# Revit family: Drain_Trench-Zurn-Z874-U-9-HDG
name_source: partatom
category: Plumbing Fixtures
units: mm (PartAtom-declared; Revit-internal decimal feet)

## family parameters
Always vertical = Yes
Cut with Voids When Loaded = No
Maintain Annotation Orientation = No
OmniClass Number = 23.70.50.21.24.14
OmniClass Title = Deck Waste Water Drains
Part Type = Normal
Room Calculation Point = No
Round Connector Dimension = Use Radius
Shared = No
Work Plane-Based = No

## types (7) — shared parameters
Assembly Code = D2040300
CW Connection = No
Connector Visibility = No
Default Elevation = 20 "
Description = UTILITY TRENCH W/ GALVANIZED STEEL FRAME 9 INCH THROAT WIDTH & COVER
HW Connection = No
Manufacturer = Zurn Water, LLC
Manufacurer Brand = Zurn
Model = Z874-U-9-HDG
Modified Date = 03/06/2026
Product Documentation Link = https://files.zurn.com
Product Page URL = https://www.zurn.com
Product data url = https://www.bimobject.com
URL = www.zurn.com
Vent Connection = No
WFU = 1
Waste Connection = Yes
zero-valued in all types: CWFU, HWFU

## per-type parameters (varying)
| type | Bottom Outlet | Connector Radius | End Outlet | Pipe Size_A Inside Diameter | Pipe Size_A Nominal Diameter | Pipe Size_A Outer Diameter | Rotation Angle | Type Comments |
| Z874-U-9-HDG E2 | No | 1 " | Yes | 2.067 " | 2 " | 2.375 " | 90.00° | Z874-U-9-HDG With 2 Inch No-Hub End outlet |
| Z874-U-9-HDG E4 | No | 2 " | Yes | 4.026 " | 4 " | 4.5 " | 90.00° | Z874-U-9-HDG With 4 Inch No-Hub End outlet |
| Z874-U-9-HDG E6 | No | 3 " | Yes | 6.065 " | 6 " | 6.625 " | 90.00° | Z874-U-9-HDG With 6 Inch No-Hub End outlet |
| Z874-U-9-HDG E8 | No | 4 " | Yes | 7.981 " | 8 " | 8.625 " | 90.00° | Z874-U-9-HDG With 8 Inch No-Hub End outlet |
| Z874-U-9-HDG U4 | Yes | 2 " | No | 4.026 " | 4 " | 4.5 " | 180.00° | Z874-U-9-HDG With 4 Inch No-Hub Bottom outlet |
| Z874-U-9-HDG U6 | Yes | 3 " | No | 6.065 " | 6 " | 6.625 " | 180.00° | Z874-U-9-HDG With 6 Inch No-Hub Bottom outlet |
| Z874-U-9-HDG U8 | Yes | 4 " | No | 7.981 " | 8 " | 8.625 " | 180.00° | Z874-U-9-HDG With 8 Inch No-Hub Bottom outlet |

## geometry (parser evidence)
native form markers: Blend x4, Sweep x5
no freeform markers — native parametric forms only
